# Revit family: 910-21-001
name_source: partatom
category: Pipe Accessories
units: mm (PartAtom-declared; Revit-internal decimal feet)

## family parameters
Always vertical = Yes
Cut with Voids When Loaded = No
Part Type = Valve - Breaks Into
Round Connector Dimension = Use Diameter
Shared = No
Work Plane-Based = No

## types (14) — shared parameters
DN100_PN10/16 = 910-0100-21-011020004
DN125_PN10/16 = 910-0125-21-011020004
DN150_PN10/16 = 910-0150-21-011020004
DN200 = No
DN200_PN10 = 910-0200-21-011020004
DN200_PN16 = 910-0200-21-311020004
DN250_PN10 = 910-0250-21-011020004
DN250_PN16 = 910-0250-21-311020004
DN300_PN10 = 910-0300-21-011020004
DN300_PN16 = 910-0300-21-311020004
DN350_PN10 = 910-0350-21-011020004
DN350_PN16 = 910-0350-21-311020004
DN400_PN10 = 910-0400-21-011020004
DN400_PN16 = 910-0400-21-311020004
DN450_PN10 = 910-0450-21-011020004
DN450_PN16 = 910-0450-21-311020004
DN500_PN10 = 910-0500-21-011020004
DN500_PN16 = 910-0500-21-311020004
DN50_PN10/16 = 910-0050-21-011020004
DN600_PN10 = 910-0600-21-011020004
DN600_PN16 = 910-0600-21-311020004
DN65 = No
DN65_PN10/16 = 910-0065-21-011020004
DN80_PN10/16 = 910-0080-21-011020004
Description_ = AVK Y-STRAINER
RF_Thick = 3 mm  [stored 0.00984252 ft]
Search_Table = 910-21-001
zero-valued in all types: Flange_Thickness_gap

## per-type parameters (varying)
- DN100: Bottom_Flange=74 mm; Bottom_Flange_Tickness=13 mm  [stored 0.0426509 ft]; D=115 mm; DN=100 mm; DN100=Yes; DN125=No; DN150=No; DN250=No; DN300=No; DN350=No; DN400=No; DN450=No; DN50=No; DN500=No; DN600=No; DN80=No; Dia_1=63 mm  [stored 0.206693 ft]; Distance_1=45 mm  [stored 0.147638 ft]; Distance_2=50 mm  [stored 0.164042 ft]; Distance_3=21 mm  [stored 0.0688976 ft]; Distance_4=151 mm; H=234 mm; Hole=20 mm  [stored 0.0656168 ft]; ID=50 mm  [stored 0.164042 ft]; L=305 mm; L2=153 mm; L5=19 mm  [stored 0.062336 ft]; L_Ref=366 mm; Nominal_Diameter=100 mm; RF=78 mm; Radius=250 mm; Rib_Height=90 mm; Rib_Thickness=10 mm  [stored 0.0328084 ft]; URL product pages=https://www.avkvalves.com
- DN065: Bottom_Flange=50 mm  [stored 0.164042 ft]; Bottom_Flange_Tickness=8 mm  [stored 0.0262467 ft]; D=93 mm; DN=65 mm  [stored 0.213255 ft]; DN100=No; DN125=No; DN150=No; DN250=No; DN300=No; DN350=No; DN400=No; DN450=No; DN50=Yes; DN500=No; DN600=No; DN80=No; Dia_1=45 mm  [stored 0.147638 ft]; Distance_1=50 mm  [stored 0.164042 ft]; Distance_2=54 mm  [stored 0.177165 ft]; Distance_3=10 mm  [stored 0.0328084 ft]; Distance_4=104 mm; H=161 mm; Hole=10 mm  [stored 0.0328084 ft]; ID=33 mm  [stored 0.108268 ft]; L=241 mm; L2=121 mm; L5=19 mm  [stored 0.062336 ft]; L_Ref=289 mm; Nominal_Diameter=65 mm  [stored 0.213255 ft]; RF=59 mm; Radius=180 mm; Rib_Height=55 mm  [stored 0.180446 ft]; Rib_Thickness=10 mm  [stored 0.0328084 ft]; URL product pages=https://www.avkvalves.com
- DN080: Bottom_Flange=53 mm  [stored 0.173885 ft]; Bottom_Flange_Tickness=12 mm  [stored 0.0393701 ft]; D=100 mm; DN=80 mm; DN100=No; DN125=No; DN150=No; DN250=No; DN300=No; DN350=No; DN400=No; DN450=No; DN50=No; DN500=No; DN600=No; DN80=Yes; Dia_1=53 mm  [stored 0.173885 ft]; Distance_1=30 mm  [stored 0.0984252 ft]; Distance_2=64 mm  [stored 0.209974 ft]; Distance_3=15 mm  [stored 0.0492126 ft]; Distance_4=124 mm; H=191 mm; Hole=15 mm  [stored 0.0492126 ft]; ID=40 mm  [stored 0.131234 ft]; L=283 mm; L2=142 mm; L5=19 mm  [stored 0.062336 ft]; L_Ref=340 mm; Nominal_Diameter=80 mm; RF=66 mm  [stored 0.216535 ft]; Radius=210 mm; Rib_Height=70 mm; Rib_Thickness=10 mm  [stored 0.0328084 ft]; URL product pages=https://www.avkvalves.com
- DN125: Bottom_Flange=81 mm; Bottom_Flange_Tickness=19 mm  [stored 0.062336 ft]; D=125 mm; DN=125 mm; DN100=No; DN125=Yes; DN150=No; DN250=No; DN300=No; DN350=No; DN400=No; DN450=No; DN50=No; DN500=No; DN600=No; DN80=No; Dia_1=76 mm; Distance_1=65 mm  [stored 0.213255 ft]; Distance_2=65 mm  [stored 0.213255 ft]; Distance_3=30 mm  [stored 0.0984252 ft]; Distance_4=147 mm; H=260 mm; Hole=25 mm  [stored 0.082021 ft]; ID=63 mm  [stored 0.206693 ft]; L=381 mm; L2=191 mm; L5=19 mm  [stored 0.062336 ft]; L_Ref=457 mm; Nominal_Diameter=125 mm; RF=92 mm; Radius=270 mm; Rib_Height=115 mm; Rib_Thickness=10 mm  [stored 0.0328084 ft]; URL product pages=https://www.avkvalves.com
https://www.avkvalves.com
 https://www.avkvalves.com
- DN150: Bottom_Flange=90 mm; Bottom_Flange_Tickness=23 mm  [stored 0.0754593 ft]; D=143 mm; DN=150 mm; DN100=No; DN125=No; DN150=Yes; DN250=No; DN300=No; DN350=No; DN400=No; DN450=No; DN50=No; DN500=No; DN600=No; DN80=No; Dia_1=89 mm; Distance_1=60 mm  [stored 0.19685 ft]; Distance_2=100 mm; Distance_3=10 mm  [stored 0.0328084 ft]; Distance_4=208 mm; H=310 mm; Hole=25 mm  [stored 0.082021 ft]; ID=75 mm; L=403 mm; L2=202 mm; L5=19 mm  [stored 0.062336 ft]; L_Ref=484 mm; Nominal_Diameter=150 mm; RF=106 mm; Radius=300 mm; Rib_Height=140 mm; Rib_Thickness=10 mm  [stored 0.0328084 ft]; URL product pages=https://www.avkvalves.com
- DN200: Bottom_Flange=120 mm; Bottom_Flange_Tickness=25 mm  [stored 0.082021 ft]; D=170 mm; DN=200 mm; DN100=No; DN125=No; DN150=No; DN250=Yes; DN300=No; DN350=No; DN400=No; DN450=No; DN50=No; DN500=No; DN600=No; DN80=No; Dia_1=115 mm; Distance_1=110 mm; Distance_2=100 mm; Distance_3=30 mm  [stored 0.0984252 ft]; Distance_4=257 mm; H=402 mm; Hole=35 mm  [stored 0.114829 ft]; ID=100 mm; L=521 mm; L2=261 mm; L5=20 mm  [stored 0.0656168 ft]; L_Ref=625 mm; Nominal_Diameter=200 mm; RF=133 mm; Radius=320 mm; Rib_Height=190 mm; Rib_Thickness=10 mm  [stored 0.0328084 ft]; URL product pages=https://www.avkvalves.com
- DN250: Bottom_Flange=161 mm; Bottom_Flange_Tickness=20 mm  [stored 0.0656168 ft]; D=203 mm; DN=250 mm; DN100=No; DN125=No; DN150=No; DN250=Yes; DN300=No; DN350=No; DN400=No; DN450=No; DN50=No; DN500=No; DN600=No; DN80=No; Dia_1=145 mm; Distance_1=170 mm; Distance_2=130 mm; Distance_3=40 mm  [stored 0.131234 ft]; Distance_4=300 mm; H=484 mm; Hole=40 mm  [stored 0.131234 ft]; ID=125 mm; L=635 mm; L2=318 mm; L5=22 mm  [stored 0.0721785 ft]; L_Ref=762 mm; Nominal_Diameter=250 mm; RF=160 mm; Radius=550 mm; Rib_Height=240 mm; Rib_Thickness=11 mm  [stored 0.0360892 ft]; URL product pages=https://www.avkvalves.com
- DN300: Bottom_Flange=195 mm; Bottom_Flange_Tickness=20 mm  [stored 0.0656168 ft]; D=243 mm; DN=300 mm; DN100=No; DN125=No; DN150=No; DN250=No; DN300=Yes; DN350=No; DN400=No; DN450=No; DN50=No; DN500=No; DN600=No; DN80=No; Dia_1=172 mm; Distance_1=170 mm; Distance_2=130 mm; Distance_3=50 mm  [stored 0.164042 ft]; Distance_4=370 mm; H=576 mm; Hole=45 mm  [stored 0.147638 ft]; ID=150 mm; L=749 mm; L2=375 mm; L5=25 mm  [stored 0.082021 ft]; L_Ref=899 mm; Nominal_Diameter=300 mm; RF=198 mm; Radius=640 mm; Rib_Height=290 mm; Rib_Thickness=12 mm  [stored 0.0393701 ft]; URL product pages=https://www.avkvalves.com
- DN350: Bottom_Flange=225 mm; Bottom_Flange_Tickness=32 mm  [stored 0.104987 ft]; D=260 mm; DN=350 mm; DN100=No; DN125=No; DN150=No; DN250=No; DN300=No; DN350=Yes; DN400=No; DN450=No; DN50=No; DN500=No; DN600=No; DN80=No; Dia_1=210 mm; Distance_1=170 mm; Distance_2=130 mm; Distance_3=50 mm  [stored 0.164042 ft]; Distance_4=428 mm; H=660 mm; Hole=50 mm  [stored 0.164042 ft]; ID=175 mm; L=762 mm; L2=381 mm; L5=27 mm; L_Ref=914 mm; Nominal_Diameter=350 mm; RF=218 mm; Radius=650 mm; Rib_Height=340 mm; Rib_Thickness=13 mm  [stored 0.0426509 ft]; URL product pages=https://www.avkvalves.com
https://www.avkvalves.com
https://www.avkvalves.com
- DN450: Bottom_Flange=290 mm; Bottom_Flange_Tickness=23 mm  [stored 0.0754593 ft]; D=320 mm; DN=450 mm; DN100=No; DN125=No; DN150=No; DN250=No; DN300=No; DN350=No; DN400=No; DN450=Yes; DN50=No; DN500=No; DN600=No; DN80=No; Dia_1=242 mm; Distance_1=200 mm; Distance_2=150 mm; Distance_3=65 mm  [stored 0.213255 ft]; Distance_4=550 mm; H=810 mm; Hole=60 mm  [stored 0.19685 ft]; ID=225 mm; L=914 mm; L2=457 mm; L5=30 mm  [stored 0.0984252 ft]; L_Ref=1097 mm; Nominal_Diameter=450 mm; RF=274 mm; Radius=750 mm; Rib_Height=440 mm; Rib_Thickness=15 mm  [stored 0.0492126 ft]; URL product pages=https://www.avkvalves.com
- DN500: Bottom_Flange=323 mm; Bottom_Flange_Tickness=23 mm  [stored 0.0754593 ft]; D=358 mm; DN=500 mm; DN100=No; DN125=No; DN150=No; DN250=No; DN300=No; DN350=No; DN400=No; DN450=No; DN50=No; DN500=Yes; DN600=No; DN80=No; Dia_1=270 mm; Distance_1=230 mm; Distance_2=170 mm; Distance_3=65 mm  [stored 0.213255 ft]; Distance_4=600 mm; H=883 mm; Hole=65 mm  [stored 0.213255 ft]; ID=250 mm; L=991 mm; L2=496 mm; L5=32 mm  [stored 0.104987 ft]; L_Ref=1189 mm; Nominal_Diameter=500 mm; RF=305 mm; Radius=800 mm; Rib_Height=490 mm; Rib_Thickness=16 mm; URL product pages=https://www.avkvalves.com
https://www.avkvalves.com
- DN600: Bottom_Flange=397 mm; Bottom_Flange_Tickness=32 mm  [stored 0.104987 ft]; D=420 mm; DN=600 mm; DN100=No; DN125=No; DN150=No; DN250=No; DN300=No; DN350=No; DN400=No; DN450=No; DN50=No; DN500=No; DN600=Yes; DN80=No; Dia_1=320 mm; Distance_1=260 mm; Distance_2=190 mm; Distance_3=70 mm; Distance_4=675 mm; H=1020 mm; Hole=70 mm; ID=300 mm; L=1143 mm; L2=572 mm; L5=36 mm  [stored 0.11811 ft]; L_Ref=1372 mm; Nominal_Diameter=600 mm; RF=364 mm; Radius=850 mm; Rib_Height=590 mm; Rib_Thickness=18 mm  [stored 0.0590551 ft]; URL product pages=https://www.avkvalves.com
- DN400: Bottom_Flange=280 mm; Bottom_Flange_Tickness=26 mm; D=290 mm; DN=400 mm; DN100=No; DN125=No; DN150=No; DN250=No; DN300=No; DN350=Yes; DN400=Yes; DN450=No; DN50=No; DN500=No; DN600=No; DN80=No; Dia_1=226 mm; Distance_1=170 mm; Distance_2=130 mm; Distance_3=50 mm  [stored 0.164042 ft]; Distance_4=500 mm; H=740 mm; Hole=55 mm  [stored 0.180446 ft]; ID=200 mm; L=838 mm; L2=419 mm; L5=28 mm  [stored 0.0918635 ft]; L_Ref=1006 mm; Nominal_Diameter=400 mm; RF=244 mm; Radius=700 mm; Rib_Height=390 mm; Rib_Thickness=14 mm  [stored 0.0459318 ft]; URL product pages=https://www.avkvalves.com
- DN050: Bottom_Flange=37 mm  [stored 0.121391 ft]; Bottom_Flange_Tickness=6 mm  [stored 0.019685 ft]; D=83 mm; DN=50 mm  [stored 0.164042 ft]; DN100=No; DN125=No; DN150=No; DN250=No; DN300=No; DN350=No; DN400=No; DN450=No; DN50=Yes; DN500=No; DN600=No; DN80=No; Dia_1=38 mm; Distance_1=30 mm  [stored 0.0984252 ft]; Distance_2=60 mm  [stored 0.19685 ft]; Distance_3=8 mm  [stored 0.0262467 ft]; Distance_4=85 mm; H=161 mm; Hole=10 mm  [stored 0.0328084 ft]; ID=25 mm  [stored 0.082021 ft]; L=216 mm; L2=108 mm; L5=19 mm  [stored 0.062336 ft]; L_Ref=259 mm; Nominal_Diameter=50 mm  [stored 0.164042 ft]; RF=50 mm  [stored 0.164042 ft]; Radius=130 mm; Rib_Height=40 mm  [stored 0.131234 ft]; Rib_Thickness=10 mm  [stored 0.0328084 ft]; URL product pages=https://www.avkvalves.com

note: [stored X ft] marks values corroborated as IEEE doubles in the binary element streams (Revit-internal decimal feet)

## geometry (parser evidence)
native form markers: Sweep x36
no freeform markers — native parametric forms only
